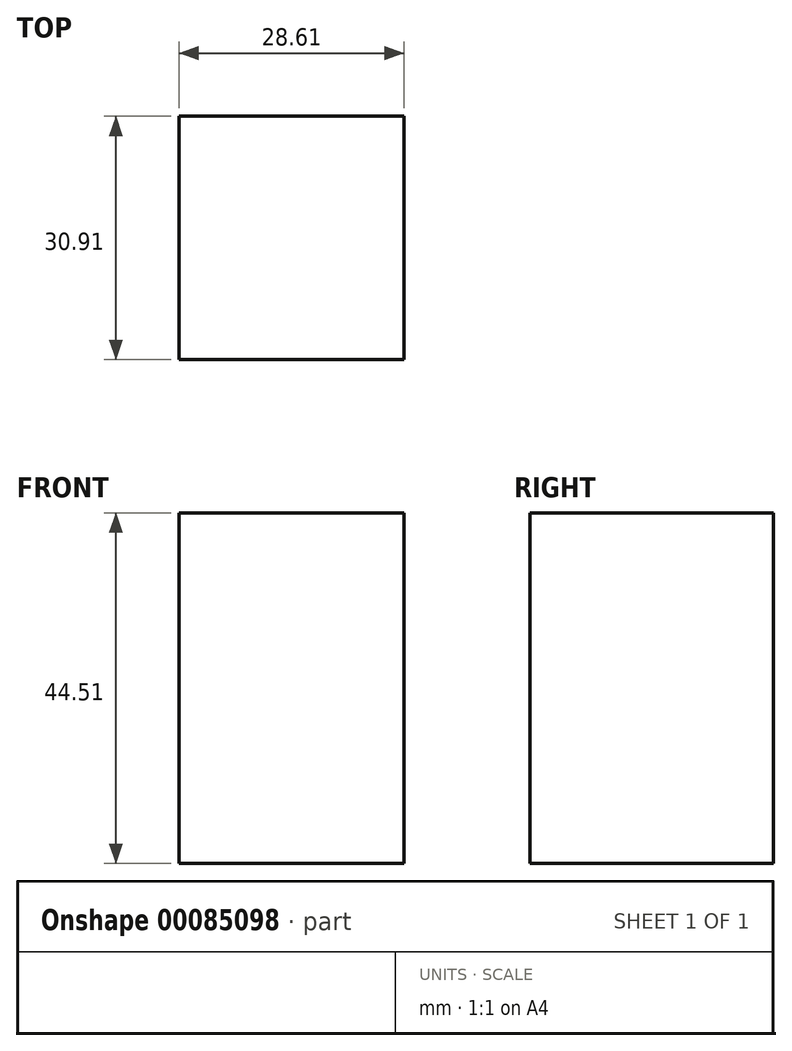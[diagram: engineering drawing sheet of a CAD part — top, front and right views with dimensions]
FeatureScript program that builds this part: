
annotation { "Feature Type Name" : "Feature", "Feature Type Description" : "" }
export const myFeature = defineFeature(function(context is Context, id is Id, definition is map)
    precondition{}
    {
        {
            var Q0;
            Q0=qCreatedBy(makeId("Front.planeOp"),FACE);
            var sketch = newSketch(context, id + "F0", { "sketchPlane" : qUnion([Q0])});
            skLineSegment(sketch, "E0.bottom", {"start": v(-44.4, 50.76) * mm, "end": v(-15.8, 50.76) * mm});
            skLineSegment(sketch, "E0.top", {"start": v(-44.4, 6.25) * mm, "end": v(-15.8, 6.25) * mm});
            skLineSegment(sketch, "E0.left", {"start": v(-44.4, 50.76) * mm, "end": v(-44.4, 6.25) * mm});
            skLineSegment(sketch, "E0.right", {"start": v(-15.8, 50.76) * mm, "end": v(-15.8, 6.25) * mm});
            skSolve(sketch);
        }
        {
            var Q0;
            Q0=makeQuery(id+"F0.imprint","IMPRINT",FACE,{"disambiguationData":[TD([[makeQuery(id+"F0.imprint","IMPRINT",EDGE,{"derivedFrom":sQuery(id+"F0.wireOp",EDGE,"E0.bottom")}),-1.0]])]});
            extrude(context, id + "F1", {"entities" : qUnion([Q0]), "depth" : 30.91 * mm});
        }
    });
